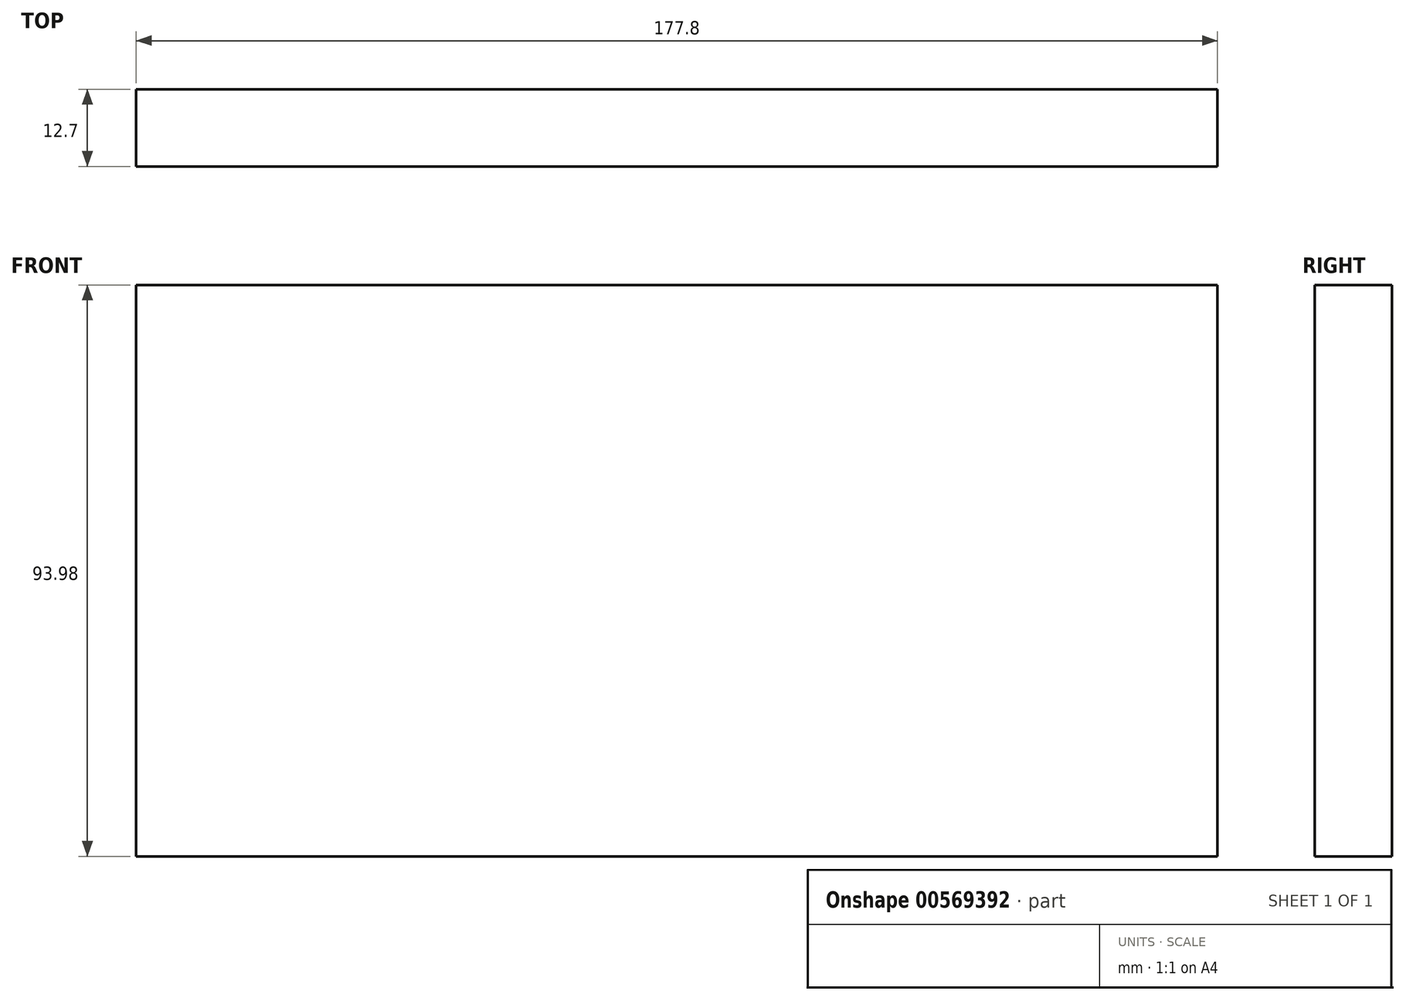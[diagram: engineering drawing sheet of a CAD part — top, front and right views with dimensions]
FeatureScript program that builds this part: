
annotation { "Feature Type Name" : "Feature", "Feature Type Description" : "" }
export const myFeature = defineFeature(function(context is Context, id is Id, definition is map)
    precondition{}
    {
        {
            var Q0;
            Q0=qCreatedBy(makeId("Front.planeOp"),FACE);
            var sketch = newSketch(context, id + "F0", { "sketchPlane" : qUnion([Q0])});
            skLineSegment(sketch, "E0.bottom", {"start": v(-62.95, 45.33) * mm, "end": v(114.85, 45.33) * mm});
            skLineSegment(sketch, "E0.top", {"start": v(-62.95, -48.65) * mm, "end": v(114.85, -48.65) * mm});
            skLineSegment(sketch, "E0.left", {"start": v(-62.95, 45.33) * mm, "end": v(-62.95, -48.65) * mm});
            skLineSegment(sketch, "E0.right", {"start": v(114.85, 45.33) * mm, "end": v(114.85, -48.65) * mm});
            skSolve(sketch);
        }
        {
            var Q0;
            Q0 = qSketchRegion(id + "F0", true);
            extrude(context, id + "F1", {"entities" : qUnion([Q0]), "endBound" : BoundingType.SYMMETRIC, "depth" : 12.7 * mm, "offsetDistance" : 25.4 * mm});
        }
    });
